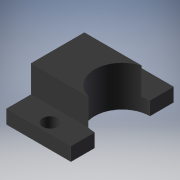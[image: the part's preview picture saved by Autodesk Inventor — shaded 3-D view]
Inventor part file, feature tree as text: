
AUTODESK INVENTOR PART (.ipt)
format: ipt  version: 2019.4 (Build 234330000, 330)  size: 130,560 bytes
history: native  units: mm
features: extrude x3, sketch x2
ambient origin geometry x8: Origin, YZ Plane, XZ Plane, XY Plane, X Axis, Y Axis, Z Axis, Center Point
bodies: Solid1 (feature_tree)
feature tree (5):
  extrude  "Extrusion1"  Depth=15.2mm
  sketch  "Sketch2"  dims[d2=5.0mm d3=5.0mm d4=1.5mm d5=1.5mm d6=2.3mm d7=2.3mm d9=6.0mm d10=0.0mm d11=9.56mm d12=8.2mm d13=7.6mm d14=3.65mm d15=4.0mm d16=0.0mm d17=4.0mm d18=0.0mm d19=3.65mm]
  extrude  "Extrusion2"  Depth=3.65mm
  extrude  "Extrusion3"  Depth=3.65mm
  sketch  "Sketch1"  dims[d0=15.2mm d1=11.28mm]
